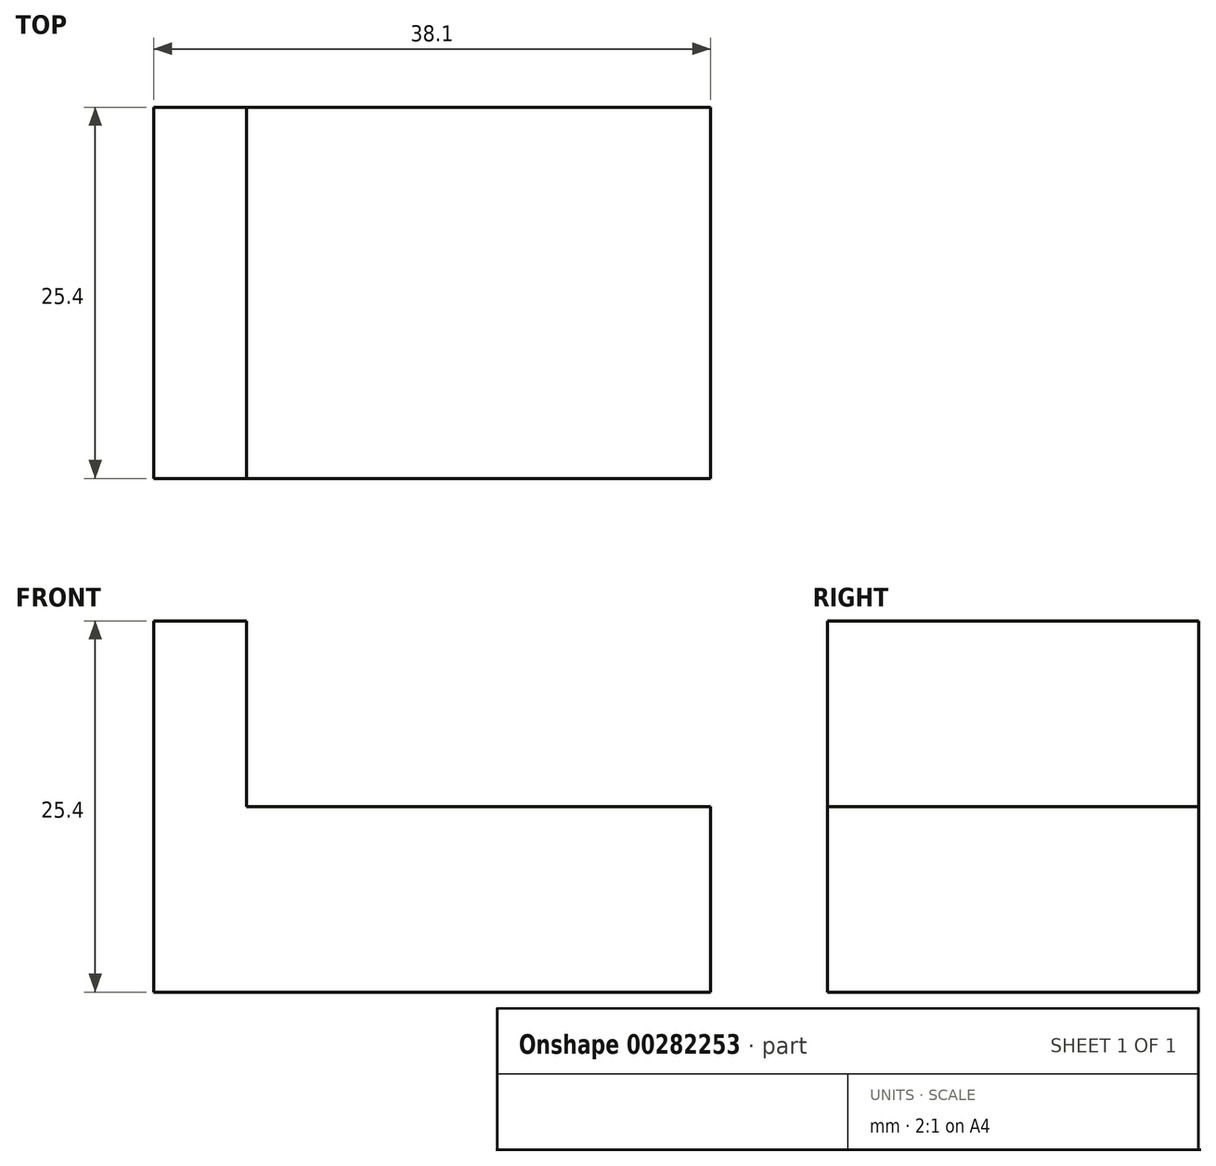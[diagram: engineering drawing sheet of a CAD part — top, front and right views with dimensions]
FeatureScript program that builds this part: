
annotation { "Feature Type Name" : "Feature", "Feature Type Description" : "" }
export const myFeature = defineFeature(function(context is Context, id is Id, definition is map)
    precondition{}
    {
        {
            var Q0;
            Q0=qCreatedBy(makeId("Front.planeOp"),FACE);
            var sketch = newSketch(context, id + "F0", { "sketchPlane" : qUnion([Q0])});
            skLineSegment(sketch, "E0", {"start": v(0, 0) * mm, "end": v(-38.1, 0) * mm});
            skLineSegment(sketch, "E1", {"start": v(-38.1, 0) * mm, "end": v(-38.1, 25.4) * mm});
            skLineSegment(sketch, "E2", {"start": v(-38.1, 25.4) * mm, "end": v(-31.75, 25.4) * mm});
            skLineSegment(sketch, "E3", {"start": v(-31.75, 25.4) * mm, "end": v(-31.75, 12.7) * mm});
            skLineSegment(sketch, "E4", {"start": v(-31.75, 12.7) * mm, "end": v(0, 12.7) * mm});
            skLineSegment(sketch, "E5", {"start": v(0, 12.7) * mm, "end": v(0, 0) * mm});
            skSolve(sketch);
        }
        {
            var Q0;
            Q0 = qSketchRegion(id + "F0", true);
            extrude(context, id + "F1", {"entities" : qUnion([Q0]), "depth" : 25.4 * mm});
        }
    });
